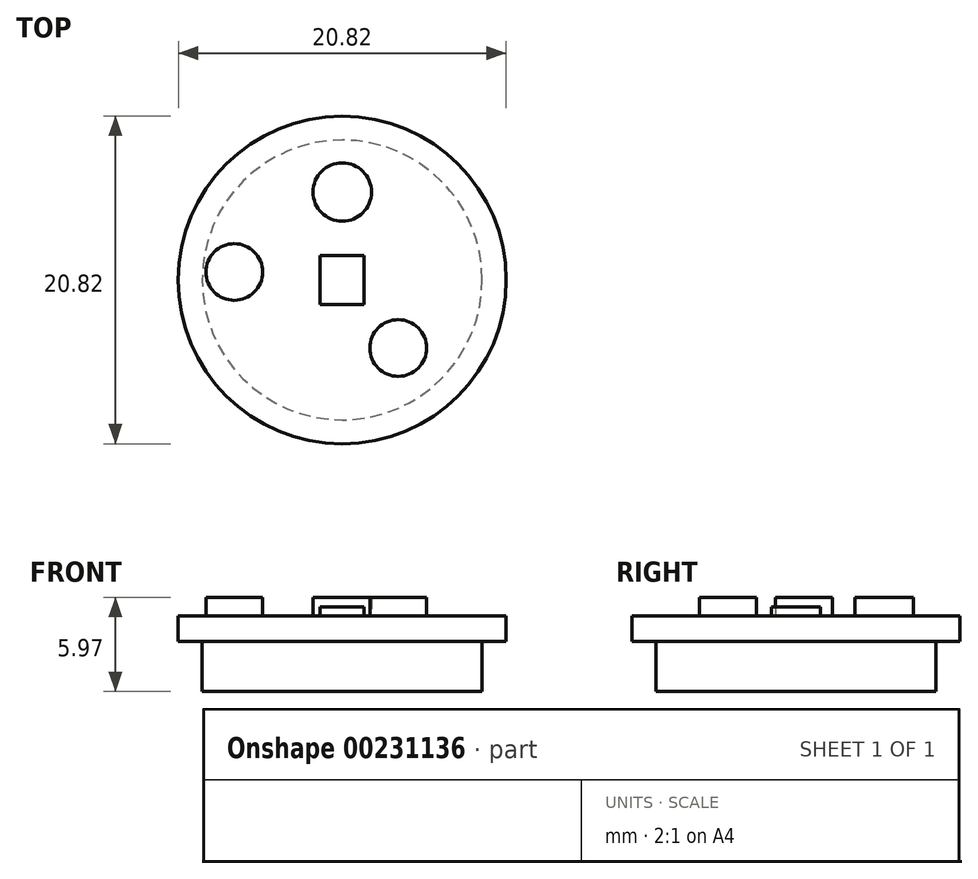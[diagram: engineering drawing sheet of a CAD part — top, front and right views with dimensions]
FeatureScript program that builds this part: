
annotation { "Feature Type Name" : "Feature", "Feature Type Description" : "" }
export const myFeature = defineFeature(function(context is Context, id is Id, definition is map)
    precondition{}
    {
        {
            var Q0;
            Q0=qCreatedBy(makeId("Top.planeOp"),FACE);
            var sketch = newSketch(context, id + "F0", { "sketchPlane" : qUnion([Q0])});
            skCircle(sketch, "E0", {"center": v(0, 0) * mm, "radius": 10.41 * mm});
            skSolve(sketch);
        }
        {
            var Q0;
            Q0=qSketchRegion(id+"F0",true);
            extrude(context, id + "F1", {"entities" : qUnion([Q0]), "depth" : 1.6 * mm});
        }
        {
            var Q0;
            Q0=makeQuery(id+"F1.opExtrude","CAP_FACE",FACE,{"disambiguationData":[OSD([sQuery(id+"F0.wireOp",EDGE,"E0")])],"isStart":true});
            var sketch = newSketch(context, id + "F2", { "sketchPlane" : qUnion([Q0])});
            skCircle(sketch, "E1", {"center": v(0, 0) * mm, "radius": 8.9 * mm});
            skSolve(sketch);
        }
        {
            var Q0;
            Q0=qSketchRegion(id+"F2",true);
            extrude(context, id + "F3", {"entities" : qUnion([Q0]), "operationType" : NewBodyOperationType.ADD, "depth" : 3.17 * mm});
        }
        {
            var Q0;
            Q0=makeQuery(id+"F1.opExtrude","CAP_FACE",FACE,{"disambiguationData":[OSD([sQuery(id+"F0.wireOp",EDGE,"E0")])],"isStart":false});
            var sketch = newSketch(context, id + "F4", { "sketchPlane" : qUnion([Q0])});
            skCircle(sketch, "E2", {"center": v(0, 5.59) * mm, "radius": 1.86 * mm});
            skCircle(sketch, "E3", {"center": v(3.56, -4.32) * mm, "radius": 1.8 * mm});
            skCircle(sketch, "E4", {"center": v(-6.86, 0.5) * mm, "radius": 1.8 * mm});
            skSolve(sketch);
        }
        {
            var Q0;
            Q0=qSketchRegion(id+"F4",true);
            extrude(context, id + "F5", {"entities" : qUnion([Q0]), "operationType" : NewBodyOperationType.ADD, "depth" : 1.2 * mm});
        }
        {
            var Q0;
            Q0=makeQuery(id+"F1.opExtrude","CAP_FACE",FACE,{"disambiguationData":[OSD([sQuery(id+"F0.wireOp",EDGE,"E0")])],"isStart":false});
            var sketch = newSketch(context, id + "F6", { "sketchPlane" : qUnion([Q0])});
            skLineSegment(sketch, "E5.bottom", {"start": v(-1.4, -1.55) * mm, "end": v(1.4, -1.55) * mm});
            skLineSegment(sketch, "E5.top", {"start": v(-1.4, 1.55) * mm, "end": v(1.4, 1.55) * mm});
            skLineSegment(sketch, "E5.left", {"start": v(-1.4, -1.55) * mm, "end": v(-1.4, 1.55) * mm});
            skLineSegment(sketch, "E5.right", {"start": v(1.4, -1.55) * mm, "end": v(1.4, 1.55) * mm});
            skSolve(sketch);
        }
        {
            var Q0;
            Q0=qSketchRegion(id+"F6",true);
            extrude(context, id + "F7", {"entities" : qUnion([Q0]), "operationType" : NewBodyOperationType.ADD, "depth" : .6 * mm});
        }
    });
